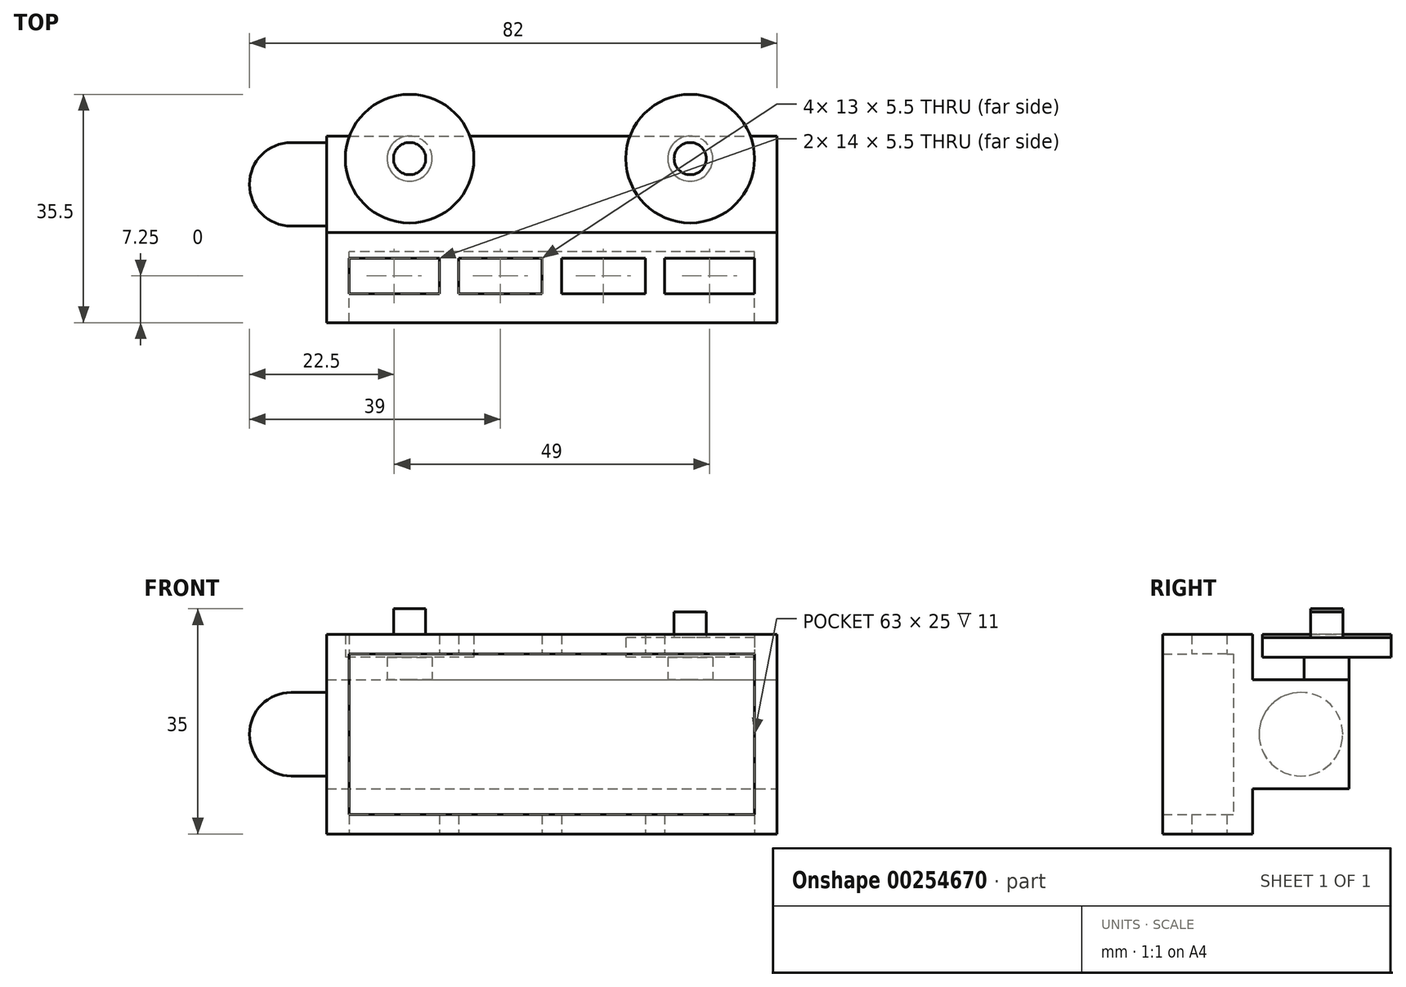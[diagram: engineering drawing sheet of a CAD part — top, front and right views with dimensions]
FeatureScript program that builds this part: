
annotation { "Feature Type Name" : "Feature", "Feature Type Description" : "" }
export const myFeature = defineFeature(function(context is Context, id is Id, definition is map)
    precondition{}
    {
        {
            var Q0;
            Q0=qCreatedBy(makeId("Front.planeOp"),FACE);
            var sketch = newSketch(context, id + "F0", { "sketchPlane" : qUnion([Q0])});
            skLineSegment(sketch, "E0.bottom", {"start": v(-35, 15.5) * mm, "end": v(35, 15.5) * mm});
            skLineSegment(sketch, "E0.top", {"start": v(-35, -15.5) * mm, "end": v(35, -15.5) * mm});
            skLineSegment(sketch, "E0.left", {"start": v(-35, 15.5) * mm, "end": v(-35, -15.5) * mm});
            skLineSegment(sketch, "E0.right", {"start": v(35, 15.5) * mm, "end": v(35, -15.5) * mm});
            skPoint(sketch, "E0.middle", {"position": v(0, 0) * mm});
            skSolve(sketch);
        }
        {
            var Q0;
            Q0=makeQuery(id+"F0.imprint","IMPRINT",FACE,{"disambiguationData":[TD([[makeQuery(id+"F0.imprint","IMPRINT",EDGE,{"derivedFrom":sQuery(id+"F0.wireOp",EDGE,"E0.bottom")}),-1.0]])]});
            extrude(context, id + "F1", {"entities" : qUnion([Q0]), "endBound" : BoundingType.SYMMETRIC, "depth" : 3 * mm});
        }
        {
            var Q0;
            Q0=makeQuery(id+"F1.opExtrude","CAP_FACE",FACE,{"disambiguationData":[OSD([sQuery(id+"F0.wireOp",EDGE,"E0.bottom"),sQuery(id+"F0.wireOp",EDGE,"E0.top"),sQuery(id+"F0.wireOp",EDGE,"E0.left"),sQuery(id+"F0.wireOp",EDGE,"E0.right")])],"isStart":false});
            var sketch = newSketch(context, id + "F2", { "sketchPlane" : qUnion([Q0])});
            skLineSegment(sketch, "E1.bottom", {"start": v(-35, -15.5) * mm, "end": v(35, -15.5) * mm});
            skLineSegment(sketch, "E1.top", {"start": v(-35, -12.5) * mm, "end": v(35, -12.5) * mm});
            skLineSegment(sketch, "E1.left", {"start": v(-35, -15.5) * mm, "end": v(-35, -12.5) * mm});
            skLineSegment(sketch, "E1.right", {"start": v(35, -15.5) * mm, "end": v(35, -12.5) * mm});
            skSolve(sketch);
        }
        {
            var Q0;
            Q0=makeQuery(id+"F2.imprint","IMPRINT",FACE,{"disambiguationData":[TD([[makeQuery(id+"F2.imprint","IMPRINT",EDGE,{"derivedFrom":sQuery(id+"F2.wireOp",EDGE,"E1.bottom")}),1.0]])]});
            extrude(context, id + "F3", {"entities" : qUnion([Q0]), "operationType" : NewBodyOperationType.ADD, "depth" : 11 * mm});
        }
        {
            var Q0;
            Q0=makeQuery(id+"F1.opExtrude","CAP_FACE",FACE,{"disambiguationData":[OSD([sQuery(id+"F0.wireOp",EDGE,"E0.bottom"),sQuery(id+"F0.wireOp",EDGE,"E0.top"),sQuery(id+"F0.wireOp",EDGE,"E0.left"),sQuery(id+"F0.wireOp",EDGE,"E0.right")])],"isStart":false});
            var sketch = newSketch(context, id + "F4", { "sketchPlane" : qUnion([Q0])});
            skLineSegment(sketch, "E2.bottom", {"start": v(35, 15.5) * mm, "end": v(-35, 15.5) * mm});
            skLineSegment(sketch, "E2.top", {"start": v(35, 12.5) * mm, "end": v(-35, 12.5) * mm});
            skLineSegment(sketch, "E2.left", {"start": v(35, 15.5) * mm, "end": v(35, 12.5) * mm});
            skLineSegment(sketch, "E2.right", {"start": v(-35, 15.5) * mm, "end": v(-35, 12.5) * mm});
            skSolve(sketch);
        }
        {
            var Q0;
            Q0=makeQuery(id+"F4.imprint","IMPRINT",FACE,{"disambiguationData":[TD([[makeQuery(id+"F4.imprint","IMPRINT",EDGE,{"derivedFrom":sQuery(id+"F4.wireOp",EDGE,"E2.bottom")}),-1.0]])]});
            extrude(context, id + "F5", {"entities" : qUnion([Q0]), "operationType" : NewBodyOperationType.ADD, "depth" : 11 * mm});
        }
        {
            var Q0;
            Q0=makeQuery(id+"F1.opExtrude","CAP_FACE",FACE,{"disambiguationData":[OSD([sQuery(id+"F0.wireOp",EDGE,"E0.bottom"),sQuery(id+"F0.wireOp",EDGE,"E0.top"),sQuery(id+"F0.wireOp",EDGE,"E0.left"),sQuery(id+"F0.wireOp",EDGE,"E0.right")])],"isStart":false});
            var sketch = newSketch(context, id + "F6", { "sketchPlane" : qUnion([Q0])});
            skLineSegment(sketch, "E3.bottom", {"start": v(35, 12.5) * mm, "end": v(31.5, 12.5) * mm});
            skLineSegment(sketch, "E3.top", {"start": v(35, -12.5) * mm, "end": v(31.5, -12.5) * mm});
            skLineSegment(sketch, "E3.left", {"start": v(35, 12.5) * mm, "end": v(35, -12.5) * mm});
            skLineSegment(sketch, "E3.right", {"start": v(31.5, 12.5) * mm, "end": v(31.5, -12.5) * mm});
            skSolve(sketch);
        }
        {
            var Q0;
            Q0=makeQuery(id+"F6.imprint","IMPRINT",FACE,{"disambiguationData":[TD([[makeQuery(id+"F6.imprint","IMPRINT",EDGE,{"derivedFrom":sQuery(id+"F6.wireOp",EDGE,"E3.bottom")}),1.0]])]});
            extrude(context, id + "F7", {"entities" : qUnion([Q0]), "operationType" : NewBodyOperationType.ADD, "depth" : 11 * mm});
        }
        {
            var Q0;
            Q0=makeQuery(id+"F1.opExtrude","CAP_FACE",FACE,{"disambiguationData":[OSD([sQuery(id+"F0.wireOp",EDGE,"E0.bottom"),sQuery(id+"F0.wireOp",EDGE,"E0.top"),sQuery(id+"F0.wireOp",EDGE,"E0.left"),sQuery(id+"F0.wireOp",EDGE,"E0.right")])],"isStart":false});
            var sketch = newSketch(context, id + "F8", { "sketchPlane" : qUnion([Q0])});
            skLineSegment(sketch, "E4.bottom", {"start": v(-35, 12.5) * mm, "end": v(-31.5, 12.5) * mm});
            skLineSegment(sketch, "E4.top", {"start": v(-35, -12.5) * mm, "end": v(-31.5, -12.5) * mm});
            skLineSegment(sketch, "E4.left", {"start": v(-35, 12.5) * mm, "end": v(-35, -12.5) * mm});
            skLineSegment(sketch, "E4.right", {"start": v(-31.5, 12.5) * mm, "end": v(-31.5, -12.5) * mm});
            skSolve(sketch);
        }
        {
            var Q0;
            Q0=makeQuery(id+"F8.imprint","IMPRINT",FACE,{"disambiguationData":[TD([[makeQuery(id+"F8.imprint","IMPRINT",EDGE,{"derivedFrom":sQuery(id+"F8.wireOp",EDGE,"E4.bottom")}),1.0]])]});
            extrude(context, id + "F9", {"entities" : qUnion([Q0]), "operationType" : NewBodyOperationType.ADD, "depth" : 11 * mm});
        }
        {
            var Q0;
            Q0=makeQuery(id+"F1.opExtrude","CAP_FACE",FACE,{"disambiguationData":[OSD([sQuery(id+"F0.wireOp",EDGE,"E0.bottom"),sQuery(id+"F0.wireOp",EDGE,"E0.top"),sQuery(id+"F0.wireOp",EDGE,"E0.left"),sQuery(id+"F0.wireOp",EDGE,"E0.right")])],"isStart":true});
            var sketch = newSketch(context, id + "F10", { "sketchPlane" : qUnion([Q0])});
            skLineSegment(sketch, "E5.bottom", {"start": v(35, 8.5) * mm, "end": v(-35, 8.5) * mm});
            skLineSegment(sketch, "E5.top", {"start": v(35, -8.5) * mm, "end": v(-35, -8.5) * mm});
            skLineSegment(sketch, "E5.left", {"start": v(35, 8.5) * mm, "end": v(35, -8.5) * mm});
            skLineSegment(sketch, "E5.right", {"start": v(-35, 8.5) * mm, "end": v(-35, -8.5) * mm});
            skPoint(sketch, "E5.middle", {"position": v(0, 0) * mm});
            skSolve(sketch);
        }
        {
            var Q0;
            Q0=makeQuery(id+"F10.imprint","IMPRINT",FACE,{"disambiguationData":[TD([[makeQuery(id+"F10.imprint","IMPRINT",EDGE,{"derivedFrom":sQuery(id+"F10.wireOp",EDGE,"E5.bottom")}),1.0]])]});
            extrude(context, id + "F11", {"entities" : qUnion([Q0]), "operationType" : NewBodyOperationType.ADD, "depth" : 15 * mm});
        }
        {
            var Q0;
            Q0=makeQuery(id+"F3.boolean.opBoolean","MERGE",FACE,{"derivedFrom":[makeQuery(id+"F1.opExtrude","SWEPT_FACE",FACE,{"disambiguationData":[OSD([sQuery(id+"F0.wireOp",EDGE,"E0.top")])]}),makeQuery(id+"F3.opExtrude","SWEPT_FACE",FACE,{"disambiguationData":[OSD([sQuery(id+"F2.wireOp",EDGE,"E1.bottom")])]})]});
            var sketch = newSketch(context, id + "F12", { "sketchPlane" : qUnion([Q0])});
            skLineSegment(sketch, "E6.bottom", {"start": v(31.5, 2.5) * mm, "end": v(17.5, 2.5) * mm});
            skLineSegment(sketch, "E6.top", {"start": v(31.5, 8) * mm, "end": v(17.5, 8) * mm});
            skLineSegment(sketch, "E6.left", {"start": v(31.5, 2.5) * mm, "end": v(31.5, 8) * mm});
            skLineSegment(sketch, "E6.right", {"start": v(17.5, 2.5) * mm, "end": v(17.5, 8) * mm});
            skPoint(sketch, "E6.middle", {"position": v(24.5, 5.25) * mm});
            skSolve(sketch);
        }
        {
            var Q0;
            Q0=makeQuery(id+"F12.imprint","IMPRINT",FACE,{"disambiguationData":[TD([[makeQuery(id+"F12.imprint","IMPRINT",EDGE,{"derivedFrom":sQuery(id+"F12.wireOp",EDGE,"E6.bottom")}),-1.0]])]});
            extrude(context, id + "F13", {"entities" : qUnion([Q0]), "operationType" : NewBodyOperationType.REMOVE, "oppositeDirection" : true, "depth" : 70 * mm});
        }
        {
            var Q0;
            Q0=makeQuery(id+"F3.boolean.opBoolean","MERGE",FACE,{"derivedFrom":[makeQuery(id+"F1.opExtrude","SWEPT_FACE",FACE,{"disambiguationData":[OSD([sQuery(id+"F0.wireOp",EDGE,"E0.top")])]}),makeQuery(id+"F3.opExtrude","SWEPT_FACE",FACE,{"disambiguationData":[OSD([sQuery(id+"F2.wireOp",EDGE,"E1.bottom")])]})]});
            var sketch = newSketch(context, id + "F14", { "sketchPlane" : qUnion([Q0])});
            skLineSegment(sketch, "E7.bottom", {"start": v(14.5, 2.5) * mm, "end": v(1.5, 2.5) * mm});
            skLineSegment(sketch, "E7.top", {"start": v(14.5, 8) * mm, "end": v(1.5, 8) * mm});
            skLineSegment(sketch, "E7.left", {"start": v(14.5, 2.5) * mm, "end": v(14.5, 8) * mm});
            skLineSegment(sketch, "E7.right", {"start": v(1.5, 2.5) * mm, "end": v(1.5, 8) * mm});
            skPoint(sketch, "E7.middle", {"position": v(8, 5.25) * mm});
            skSolve(sketch);
        }
        {
            var Q0;
            Q0=makeQuery(id+"F14.imprint","IMPRINT",FACE,{"disambiguationData":[TD([[makeQuery(id+"F14.imprint","IMPRINT",EDGE,{"derivedFrom":sQuery(id+"F14.wireOp",EDGE,"E7.bottom")}),-1.0]])]});
            extrude(context, id + "F15", {"entities" : qUnion([Q0]), "operationType" : NewBodyOperationType.REMOVE, "oppositeDirection" : true, "depth" : 70 * mm});
        }
        {
            var Q0;
            Q0=makeQuery(id+"F3.boolean.opBoolean","MERGE",FACE,{"derivedFrom":[makeQuery(id+"F1.opExtrude","SWEPT_FACE",FACE,{"disambiguationData":[OSD([sQuery(id+"F0.wireOp",EDGE,"E0.top")])]}),makeQuery(id+"F3.opExtrude","SWEPT_FACE",FACE,{"disambiguationData":[OSD([sQuery(id+"F2.wireOp",EDGE,"E1.bottom")])]})]});
            var sketch = newSketch(context, id + "F16", { "sketchPlane" : qUnion([Q0])});
            skLineSegment(sketch, "E8.bottom", {"start": v(-14.5, 8) * mm, "end": v(-1.5, 8) * mm});
            skLineSegment(sketch, "E8.top", {"start": v(-14.5, 2.5) * mm, "end": v(-1.5, 2.5) * mm});
            skLineSegment(sketch, "E8.left", {"start": v(-14.5, 8) * mm, "end": v(-14.5, 2.5) * mm});
            skLineSegment(sketch, "E8.right", {"start": v(-1.5, 8) * mm, "end": v(-1.5, 2.5) * mm});
            skPoint(sketch, "E8.middle", {"position": v(-8, 5.25) * mm});
            skSolve(sketch);
        }
        {
            var Q0;
            Q0=makeQuery(id+"F16.imprint","IMPRINT",FACE,{"disambiguationData":[TD([[makeQuery(id+"F16.imprint","IMPRINT",EDGE,{"derivedFrom":sQuery(id+"F16.wireOp",EDGE,"E8.bottom")}),-1.0]])]});
            extrude(context, id + "F17", {"entities" : qUnion([Q0]), "operationType" : NewBodyOperationType.REMOVE, "oppositeDirection" : true, "depth" : 70 * mm});
        }
        {
            var Q0;
            Q0=makeQuery(id+"F16.imprint","IMPRINT",FACE,{"disambiguationData":[TD([[makeQuery(id+"F16.imprint","IMPRINT",EDGE,{"derivedFrom":sQuery(id+"F16.wireOp",EDGE,"E8.bottom")}),1.0]])]});
            var sketch = newSketch(context, id + "F18", { "sketchPlane" : qUnion([Q0])});
            skLineSegment(sketch, "E9.bottom", {"start": v(-31.5, 2.5) * mm, "end": v(-17.5, 2.5) * mm});
            skLineSegment(sketch, "E9.top", {"start": v(-31.5, 8) * mm, "end": v(-17.5, 8) * mm});
            skLineSegment(sketch, "E9.left", {"start": v(-31.5, 2.5) * mm, "end": v(-31.5, 8) * mm});
            skLineSegment(sketch, "E9.right", {"start": v(-17.5, 2.5) * mm, "end": v(-17.5, 8) * mm});
            skPoint(sketch, "E9.middle", {"position": v(-24.5, 5.25) * mm});
            skSolve(sketch);
        }
        {
            var Q0;
            Q0 = qSketchRegion(id + "F18", true);
            extrude(context, id + "F19", {"entities" : qUnion([Q0]), "operationType" : NewBodyOperationType.REMOVE, "oppositeDirection" : true, "depth" : 70 * mm});
        }
        {
            var Q0;
            Q0=makeQuery(id+"F11.opExtrude","SWEPT_FACE",FACE,{"disambiguationData":[OSD([sQuery(id+"F10.wireOp",EDGE,"E5.bottom")])]});
            var sketch = newSketch(context, id + "F20", { "sketchPlane" : qUnion([Q0])});
            skSolve(sketch);
        }
        {
            var Q0;
            {var subQ0=sQuery(id+"F10.wireOp",EDGE,"E5.bottom");Q0=makeQuery(id+"F20.imprint","IMPRINT",FACE,{"disambiguationData":[TD([[makeQuery(id+"F20.imprint","IMPRINT",EDGE,{"derivedFrom":makeQuery(id+"F11.opExtrude","CAP_EDGE",EDGE,{"disambiguationData":[OSD([subQ0])],"isStart":false})}),-1.0]])]});}
            var sketch = newSketch(context, id + "F21", { "sketchPlane" : qUnion([Q0])});
            skCircle(sketch, "E10", {"center": v(21.5, 13) * mm, "radius": 3.5 * mm});
            skSolve(sketch);
        }
        {
            var Q0;
            Q0 = qSketchRegion(id + "F21", true);
            extrude(context, id + "F22", {"entities" : qUnion([Q0]), "operationType" : NewBodyOperationType.ADD, "depth" : 3.5 * mm});
        }
        {
            var Q0;
            {var subQ0=sQuery(id+"F10.wireOp",EDGE,"E5.bottom");Q0=makeQuery(id+"F20.imprint","IMPRINT",FACE,{"disambiguationData":[TD([[makeQuery(id+"F20.imprint","IMPRINT",EDGE,{"derivedFrom":makeQuery(id+"F11.opExtrude","CAP_EDGE",EDGE,{"disambiguationData":[OSD([subQ0])],"isStart":false})}),-1.0]])]});}
            var sketch = newSketch(context, id + "F23", { "sketchPlane" : qUnion([Q0])});
            skCircle(sketch, "E11", {"center": v(-22.1, 13) * mm, "radius": 3.5 * mm});
            skSolve(sketch);
        }
        {
            var Q0;
            Q0 = qSketchRegion(id + "F23", true);
            extrude(context, id + "F24", {"entities" : qUnion([Q0]), "operationType" : NewBodyOperationType.ADD, "depth" : 3.5 * mm});
        }
        {
            var Q0;
            Q0=makeQuery(id+"F22.opExtrude","CAP_FACE",FACE,{"disambiguationData":[OSD([sQuery(id+"F21.wireOp",EDGE,"E10")])],"isStart":false});
            var sketch = newSketch(context, id + "F25", { "sketchPlane" : qUnion([Q0])});
            skCircle(sketch, "E12", {"center": v(21.5, 13) * mm, "radius": 10 * mm});
            skSolve(sketch);
        }
        {
            var Q0;
            Q0 = qSketchRegion(id + "F25", true);
            extrude(context, id + "F26", {"entities" : qUnion([Q0]), "operationType" : NewBodyOperationType.ADD, "depth" : 3 * mm});
        }
        {
            var Q0;
            Q0=makeQuery(id+"F24.opExtrude","CAP_FACE",FACE,{"disambiguationData":[OSD([sQuery(id+"F23.wireOp",EDGE,"E11")])],"isStart":false});
            var sketch = newSketch(context, id + "F27", { "sketchPlane" : qUnion([Q0])});
            skCircle(sketch, "E13", {"center": v(-22.1, 13) * mm, "radius": 10 * mm});
            skSolve(sketch);
        }
        {
            var Q0;
            Q0 = qSketchRegion(id + "F27", true);
            extrude(context, id + "F28", {"entities" : qUnion([Q0]), "operationType" : NewBodyOperationType.ADD, "depth" : 3.5 * mm});
        }
        {
            var Q0;
            Q0=makeQuery(id+"F28.opExtrude","CAP_FACE",FACE,{"disambiguationData":[OSD([sQuery(id+"F27.wireOp",EDGE,"E13")])],"isStart":false});
            var sketch = newSketch(context, id + "F29", { "sketchPlane" : qUnion([Q0])});
            skCircle(sketch, "E14", {"center": v(-22.1, 13) * mm, "radius": 2.5 * mm});
            skSolve(sketch);
        }
        {
            var Q0;
            Q0 = qSketchRegion(id + "F29", true);
            extrude(context, id + "F30", {"entities" : qUnion([Q0]), "operationType" : NewBodyOperationType.ADD, "depth" : 4 * mm});
        }
        {
            var Q0;
            Q0=makeQuery(id+"F26.opExtrude","CAP_FACE",FACE,{"disambiguationData":[OSD([sQuery(id+"F25.wireOp",EDGE,"E12")])],"isStart":false});
            var sketch = newSketch(context, id + "F31", { "sketchPlane" : qUnion([Q0])});
            skCircle(sketch, "E15", {"center": v(21.5, 13) * mm, "radius": 2.5 * mm});
            skSolve(sketch);
        }
        {
            var Q0;
            Q0=makeQuery(id+"F31.imprint","IMPRINT",FACE,{"disambiguationData":[TD([[makeQuery(id+"F31.imprint","IMPRINT",EDGE,{"derivedFrom":sQuery(id+"F31.wireOp",EDGE,"E15")}),1.0]])]});
            extrude(context, id + "F32", {"entities" : qUnion([Q0]), "operationType" : NewBodyOperationType.ADD, "depth" : 4 * mm});
        }
        {
            var Q0;
            Q0=makeQuery(id+"F11.boolean.opBoolean","MERGE",FACE,{"derivedFrom":[makeQuery(id+"F9.boolean.opBoolean","MERGE",FACE,{"derivedFrom":[makeQuery(id+"F5.boolean.opBoolean","MERGE",FACE,{"derivedFrom":[makeQuery(id+"F3.boolean.opBoolean","MERGE",FACE,{"derivedFrom":[makeQuery(id+"F1.opExtrude","SWEPT_FACE",FACE,{"disambiguationData":[OSD([sQuery(id+"F0.wireOp",EDGE,"E0.left")])]}),makeQuery(id+"F3.opExtrude","SWEPT_FACE",FACE,{"disambiguationData":[OSD([sQuery(id+"F2.wireOp",EDGE,"E1.left")])]})]}),makeQuery(id+"F5.opExtrude","SWEPT_FACE",FACE,{"disambiguationData":[OSD([sQuery(id+"F4.wireOp",EDGE,"E2.right")])]})]}),makeQuery(id+"F9.opExtrude","SWEPT_FACE",FACE,{"disambiguationData":[OSD([sQuery(id+"F8.wireOp",EDGE,"E4.left")])]})]}),makeQuery(id+"F11.opExtrude","SWEPT_FACE",FACE,{"disambiguationData":[OSD([sQuery(id+"F10.wireOp",EDGE,"E5.left")])]})]});
            var sketch = newSketch(context, id + "F33", { "sketchPlane" : qUnion([Q0])});
            skCircle(sketch, "E16", {"center": v(-9, 0) * mm, "radius": 6.5 * mm});
            skPoint(sketch, "E16.centerSnap0", {"position": v(-9, 8.5) * mm});
            skSolve(sketch);
        }
        {
            var Q0;
            Q0 = qSketchRegion(id + "F33", true);
            extrude(context, id + "F34", {"entities" : qUnion([Q0]), "operationType" : NewBodyOperationType.ADD, "depth" : 5.5 * mm});
        }
        {
            var Q0;
            Q0=makeQuery(id+"F34.opExtrude","CAP_FACE",FACE,{"disambiguationData":[OSD([sQuery(id+"F33.wireOp",EDGE,"E16")])],"isStart":false});
            var sketch = newSketch(context, id + "F35", { "sketchPlane" : qUnion([Q0])});
            skLineSegment(sketch, "E17", {"start": v(-9, 0) * mm, "end": v(-2.5, 0) * mm});
            skLineSegment(sketch, "E18", {"start": v(-2.5, 0) * mm, "end": v(-15.5, 0) * mm});
            skSolve(sketch);
        }
        {
            var Q0;
            {var subQ0=sQuery(id+"F35.wireOp",EDGE,"E18");var subQ3=makeQuery(id+"F35.imprint","IMPRINT",VERTEX,{"derivedFrom":subQ0});Q0=makeQuery(id+"F35.imprint","IMPRINT",FACE,{"disambiguationData":[TD([[makeQuery(id+"F35.imprint","IMPRINT",EDGE,{"disambiguationData":[TD([[subQ3,1.0]])],"derivedFrom":subQ0}),1.0]])]});}
            var Q1;
            Q1=sQuery(id+"F35.wireOp",EDGE,"E18");
            revolve(context, id + "F36", {"operationType" : NewBodyOperationType.ADD, "entities" : qUnion([Q0]), "axis" : qUnion([Q1]), "revolveType" : RevolveType.FULL});
        }
    });
